# Revit family: INSEL LBR LED
name_source: partatom
category: Осветительные приборы
revit_build: Autodesk Revit 2016 (Build: 20150220_1215(x64)
units: mm (PartAtom-declared; Revit-internal decimal feet)

## family parameters
Источник света = Да
Общий = Нет
Основа = Грань
При загрузке вырезать с полостями = Нет
Размер круглого соединителя = Использовать диаметр
Тип детали = Нормальный
Точка расчета площади = Нет

## types (1)
- INSEL LBR LED
    ADSK_Единица измерения = Шт.
    ADSK_Завод-изготовитель = ООО МГК Световые технологии
    ADSK_Код изделия = 1332000390
    ADSK_Количество фаз = 1
    ADSK_Количество фаз числовое = 1
    ADSK_Коэффициент мощности = 0.96
    ADSK_Масса = 12.3
    ADSK_Наименование = Энергоэффективный светильник с высокой степенью IP для установки в ниши, в том числе под навесом АЗС. Рассчитан для работы в сети переменного тока 90-250 В, 50-60 Гц, в сети постоянного тока 130-430 В. Является заменой светильников типа ГВП, РВП, ЖВП. Возможно применение светильников в системе аварийного освещения с ЦСАО DIALOG
    ADSK_Напряжение = 230 В
    ADSK_Номинальная мощность = 0 кВт
    ADSK_Полная мощность = 0 кВ·А
    ADSK_Размер_Высота = 128 мм
    ADSK_Размер_Радиус = 15 мм
    ADSK_Размер_Ширина = 480 мм
    ADSK_Ток = 0 А
    ADSK_Энергоэффективность = 105 лм/Вт
    IP Class = IP66
    URL = https://www.ltcompany.com
    Блок аварийного питания = Нет
    Видимая форма излучения при визуализации = Нет
    Группа модели = Светильники
    Изготовитель = ООО МГК Световые технологии
    Излучатели = Плафон самосвечение
    Излучение по длине прямоугольника = 335 мм
    Излучение по ширине прямоугольника = 335 мм
    Класс Защиты = I
    Класс пожароопасности = П-I,II,IIa,ІІІ
    Климатическая зона = УХЛ1
    Код по классификатору = D5020200
    Корпус = Белый металл
    Корпус.ширина = 335 мм
    Область использования = Промышленные предприятия, Складские объекты, Стадионы, Транспортные узлы (вокзалы, аэропорты)
    Описание = Энергоэффективный светильник с высокой степенью IP для установки в ниши, в том числе под навесом АЗС. Рассчитан для работы в сети переменного тока 90-250 В, 50-60 Гц, в сети постоянного тока 130-430 В. Является заменой светильников типа ГВП, РВП, ЖВП. Возможно применение светильников в системе аварийного освещения с ЦСАО DIALOG
    Отметка по умолчанию = 0 мм
    Плафон = Плафон прозрачный
    Полная установленная мощность = 0 кВ·А
    Разработчик = ООО ПРОРУБИМ
    Разработчик (телефон) = +7 (495) 649-85-43
    Рама = 28 мм
    Светофильтр = 16777215
    Смещение цветовой температуры при затухании лампы = <Нет>
    Тип ИС = LED
    Тип ПРА = Драйвер
    Тип продукции = Светильник
    Угол наклона = -90.00°
    Файл фотометрической сетки = generic
